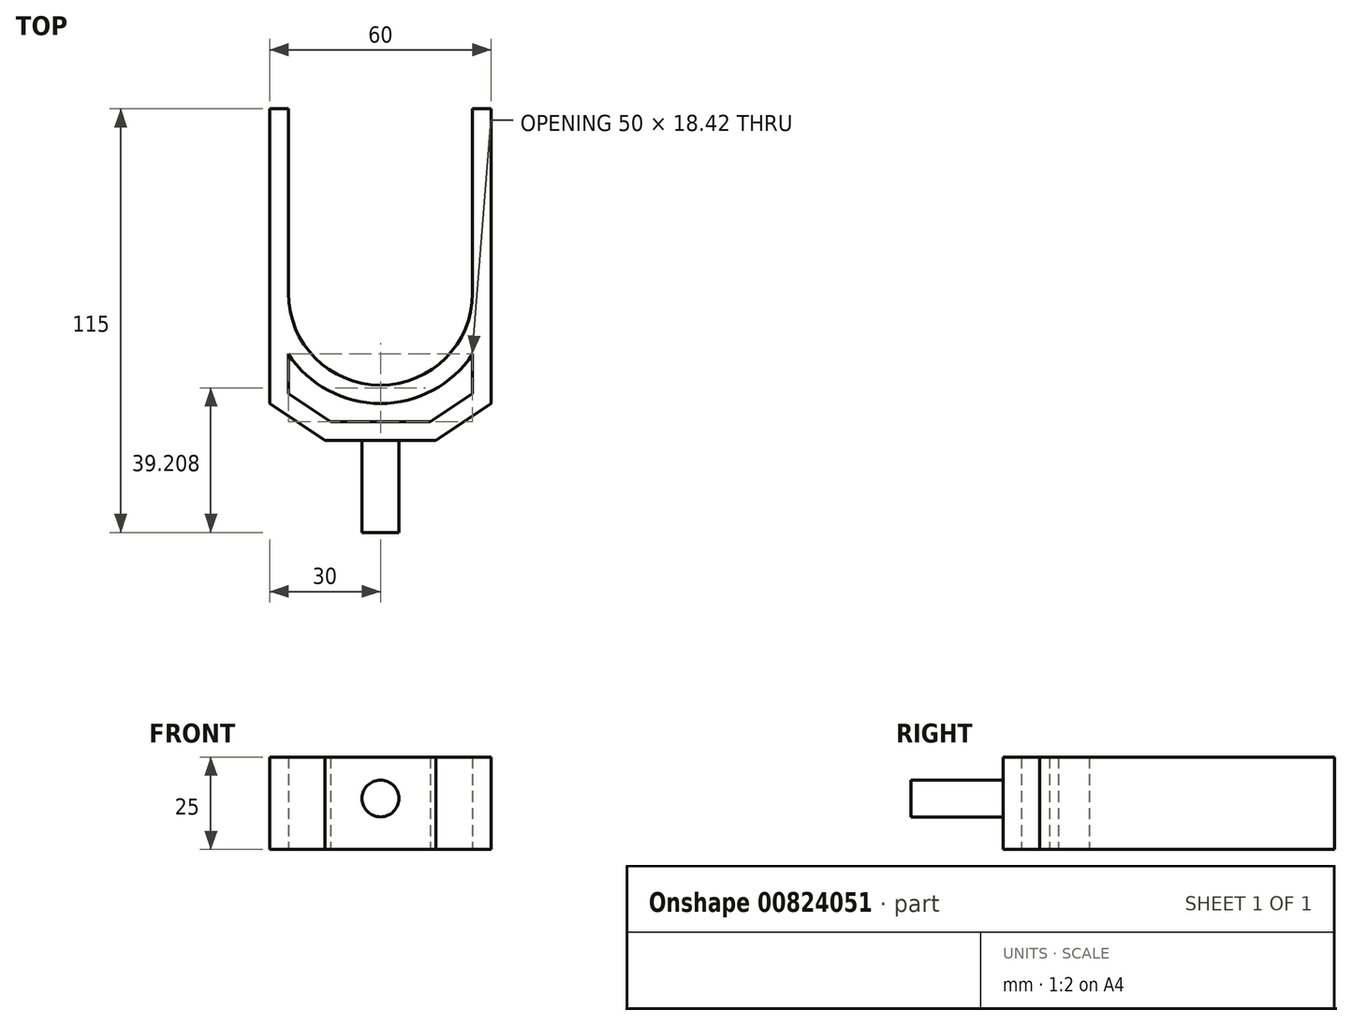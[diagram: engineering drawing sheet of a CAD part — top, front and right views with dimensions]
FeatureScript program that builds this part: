
annotation { "Feature Type Name" : "Feature", "Feature Type Description" : "" }
export const myFeature = defineFeature(function(context is Context, id is Id, definition is map)
    precondition{}
    {
        {
            var Q0;
            Q0=qCreatedBy(makeId("Top.planeOp"),FACE);
            var sketch = newSketch(context, id + "F0", { "sketchPlane" : qUnion([Q0])});
            skCircle(sketch, "E0", {"center": v(0, 0) * mm, "radius": 25 * mm, "construction": true});
            skArc(sketch, "E1", {"start": v(-25, 0) * mm, "mid": v(0, -25) * mm, "end": v(25, 0) * mm});
            skArc(sketch, "E2", {"start": v(-25, -16.58) * mm, "mid": v(0, -30) * mm, "end": v(25, -16.58) * mm});
            skLineSegment(sketch, "E3", {"start": v(-30, 0) * mm, "end": v(-30, 50) * mm});
            skLineSegment(sketch, "E4", {"start": v(-30, 50) * mm, "end": v(-25, 50) * mm});
            skLineSegment(sketch, "E5", {"start": v(30, 50) * mm, "end": v(30, 0) * mm});
            skLineSegment(sketch, "E6", {"start": v(-30, 0) * mm, "end": v(-30, -30) * mm});
            skLineSegment(sketch, "E7", {"start": v(-30, -30) * mm, "end": v(-15, -40) * mm});
            skLineSegment(sketch, "E8", {"start": v(-15, -40) * mm, "end": v(15, -40) * mm});
            skLineSegment(sketch, "E9", {"start": v(15, -40) * mm, "end": v(30, -30) * mm});
            skLineSegment(sketch, "E10", {"start": v(30, -30) * mm, "end": v(30, 0) * mm});
            skLineSegment(sketch, "E11", {"start": v(-25, 0) * mm, "end": v(-25, 50) * mm});
            skLineSegment(sketch, "E12", {"start": v(25, 0) * mm, "end": v(25, 50) * mm});
            skLineSegment(sketch, "E13.trimOffspring", {"start": v(25, 50) * mm, "end": v(30, 50) * mm});
            skLineSegment(sketch, "E14.0", {"start": v(25, -27.32) * mm, "end": v(25, -16.58) * mm});
            skLineSegment(sketch, "E14.1", {"start": v(-25, -16.58) * mm, "end": v(-25, -27.32) * mm});
            skLineSegment(sketch, "E14.2", {"start": v(-25, -27.32) * mm, "end": v(-13.49, -35) * mm});
            skLineSegment(sketch, "E14.3", {"start": v(-13.49, -35) * mm, "end": v(13.49, -35) * mm});
            skLineSegment(sketch, "E14.4", {"start": v(13.49, -35) * mm, "end": v(25, -27.32) * mm});
            skSolve(sketch);
        }
        {
            var Q0;
            Q0=makeQuery(id+"F0.imprint","IMPRINT",FACE,{"disambiguationData":[TD([[makeQuery(id+"F0.imprint","IMPRINT",EDGE,{"derivedFrom":sQuery(id+"F0.wireOp",EDGE,"E1")}),-1.0]])]});
            extrude(context, id + "F1", {"entities" : qUnion([Q0]), "depth" : 25 * mm, "offsetDistance" : 25 * mm});
        }
        {
            var Q0;
            Q0=makeQuery(id+"F1.opExtrude","SWEPT_FACE",FACE,{"disambiguationData":[OSD([sQuery(id+"F0.wireOp",EDGE,"E8")])]});
            var sketch = newSketch(context, id + "F2", { "sketchPlane" : qUnion([Q0])});
            skCircle(sketch, "E15", {"center": v(0, 13.8) * mm, "radius": 5 * mm});
            skSolve(sketch);
        }
        {
            var Q0;
            Q0=makeQuery(id+"F2.imprint","IMPRINT",FACE,{"disambiguationData":[TD([[makeQuery(id+"F2.imprint","IMPRINT",EDGE,{"derivedFrom":sQuery(id+"F2.wireOp",EDGE,"E15")}),1.0]])]});
            extrude(context, id + "F3", {"entities" : qUnion([Q0]), "operationType" : NewBodyOperationType.ADD, "depth" : 25 * mm, "offsetDistance" : 25 * mm});
        }
    });
